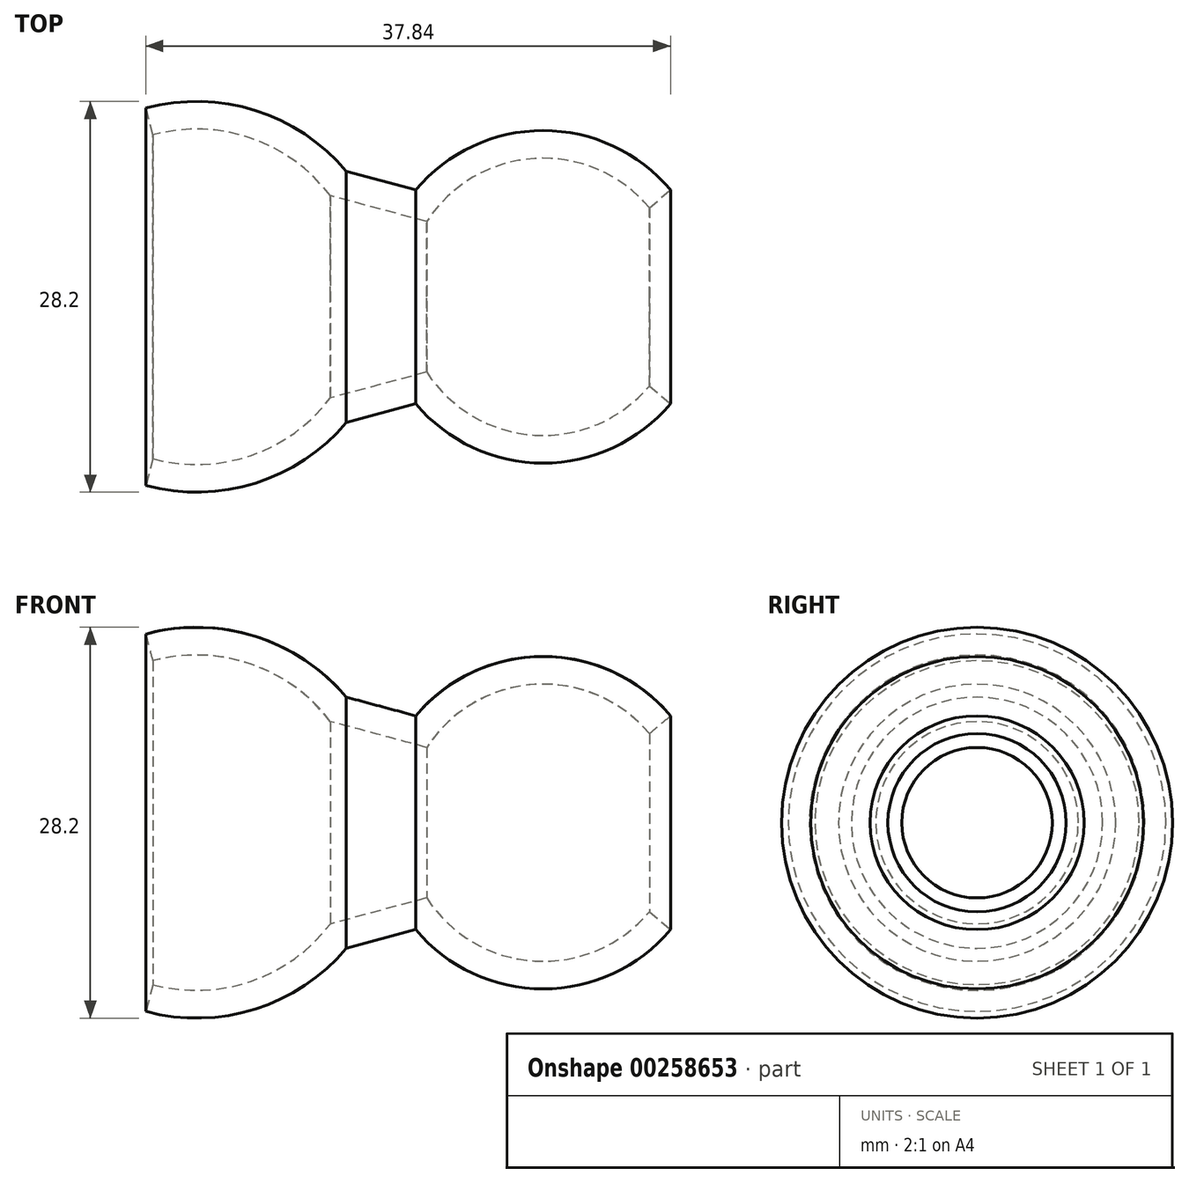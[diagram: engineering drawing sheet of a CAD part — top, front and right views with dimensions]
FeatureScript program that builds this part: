
annotation { "Feature Type Name" : "Feature", "Feature Type Description" : "" }
export const myFeature = defineFeature(function(context is Context, id is Id, definition is map)
    precondition{}
    {
        {
            var Q0;
            Q0=qCreatedBy(makeId("Top.planeOp"),FACE);
            var sketch = newSketch(context, id + "F0", { "sketchPlane" : qUnion([Q0])});
            skCircle(sketch, "E0", {"center": v(0, 0) * mm, "radius": 12.1 * mm});
            skCircle(sketch, "E1", {"center": v(25, 0) * mm, "radius": 12 * mm});
            skCircle(sketch, "E2", {"center": v(0, 0) * mm, "radius": 14.1 * mm});
            skCircle(sketch, "E3", {"center": v(25, 0) * mm, "radius": 10 * mm});
            skLineSegment(sketch, "E4", {"start": v(25, 0) * mm, "end": v(25, 27.73) * mm, "construction": true});
            skLineSegment(sketch, "E5", {"start": v(25, 0) * mm, "end": v(34.2, 7.71) * mm});
            skLineSegment(sketch, "E6", {"start": v(25, 0) * mm, "end": v(15.8, 7.71) * mm});
            skLineSegment(sketch, "E7", {"start": v(0, 0) * mm, "end": v(0, 27.73) * mm, "construction": true});
            skLineSegment(sketch, "E8", {"start": v(0, 0) * mm, "end": v(10.8, 9.06) * mm});
            skLineSegment(sketch, "E9", {"start": v(0, 0) * mm, "end": v(-3.65, 13.62) * mm});
            skLineSegment(sketch, "E10", {"start": v(10.8, 9.06) * mm, "end": v(15.8, 7.71) * mm});
            skLineSegment(sketch, "E11", {"start": v(9.65, 7.3) * mm, "end": v(16.6, 5.43) * mm});
            skLineSegment(sketch, "E12", {"start": v(0, 0) * mm, "end": v(25, 0) * mm, "construction": true});
            skLineSegment(sketch, "E13", {"start": v(0, 12.1) * mm, "end": v(-36.05, 12.1) * mm, "construction": true});
            skLineSegment(sketch, "E14", {"start": v(-3.13, 11.69) * mm, "end": v(-36.05, 11.69) * mm, "construction": true});
            skSolve(sketch);
        }
        {
            var Q0;
            {var subQ3=sQuery(id+"F0.wireOp",EDGE,"E6");var subQ5=sQuery(id+"F0.wireOp",EDGE,"E3");var subQ7=makeQuery(id+"F0.imprint","INTERSECT",VERTEX,{"derivedFrom":[subQ5,subQ3]});Q0=makeQuery(id+"F0.imprint","IMPRINT",FACE,{"disambiguationData":[TD([[makeQuery(id+"F0.imprint","IMPRINT",EDGE,{"disambiguationData":[TD([[subQ7,1.0]])],"derivedFrom":subQ5}),-1.0]])]});}
            var Q1;
            {var subQ0=sQuery(id+"F0.wireOp",EDGE,"E8");var subQ1=sQuery(id+"F0.wireOp",EDGE,"E0");var subQ2=makeQuery(id+"F0.imprint","INTERSECT",VERTEX,{"derivedFrom":[subQ1,subQ0]});Q1=makeQuery(id+"F0.imprint","IMPRINT",FACE,{"disambiguationData":[TD([[makeQuery(id+"F0.imprint","IMPRINT",EDGE,{"disambiguationData":[TD([[subQ2,-1.0]])],"derivedFrom":subQ1}),-1.0]])]});}
            var Q2;
            {var subQ0=sQuery(id+"F0.wireOp",EDGE,"E11");var subQ1=sQuery(id+"F0.wireOp",EDGE,"E0");var subQ2=makeQuery(id+"F0.imprint","INTERSECT",VERTEX,{"derivedFrom":[subQ1,subQ0]});Q2=makeQuery(id+"F0.imprint","IMPRINT",FACE,{"disambiguationData":[TD([[makeQuery(id+"F0.imprint","IMPRINT",EDGE,{"disambiguationData":[TD([[subQ2,-1.0]])],"derivedFrom":subQ1}),-1.0]])]});}
            var Q3;
            {var subQ3=sQuery(id+"F0.wireOp",EDGE,"E11");var subQ5=sQuery(id+"F0.wireOp",EDGE,"E3");var subQ7=makeQuery(id+"F0.imprint","INTERSECT",VERTEX,{"derivedFrom":[subQ5,subQ3]});Q3=makeQuery(id+"F0.imprint","IMPRINT",FACE,{"disambiguationData":[TD([[makeQuery(id+"F0.imprint","IMPRINT",EDGE,{"disambiguationData":[TD([[subQ7,1.0]])],"derivedFrom":subQ5}),-1.0]])]});}
            var Q4;
            {var subQ0=sQuery(id+"F0.wireOp",EDGE,"E10");Q4=makeQuery(id+"F0.imprint","IMPRINT",FACE,{"disambiguationData":[TD([[makeQuery(id+"F0.imprint","IMPRINT",EDGE,{"derivedFrom":subQ0}),-1.0]])]});}
            var Q5;
            Q5=sQuery(id+"F0.wireOp",EDGE,"E12");
            revolve(context, id + "F1", {"entities" : qUnion([Q0, Q1, Q2, Q3, Q4]), "axis" : qUnion([Q5]), "revolveType" : RevolveType.FULL});
        }
    });
